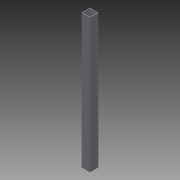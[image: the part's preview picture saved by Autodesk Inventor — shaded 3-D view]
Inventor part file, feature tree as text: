
AUTODESK INVENTOR PART (.ipt)
format: ipt  version: 2013 (Build 170138000, 138)  size: 79,872 bytes
history: native  units: in
note: dims shown in document units (in); Inventor stores cm internally (conversion verified against a paired STEP export)
features: other x2, extrude x1, sketch x1
ambient origin geometry x8: Origin, YZ Plane, XZ Plane, XY Plane, X Axis, Y Axis, Z Axis, Center Point
bodies: Solid1 (feature_tree)
feature tree (4):
  other  "Table"
  other  "Part15-01"
  extrude  "Extrusion1"  Depth=1.5in
  sketch  "Sketch1"  dims[d0=1.5in d1=1.5in d2=0.0938in d4=0.0in]
